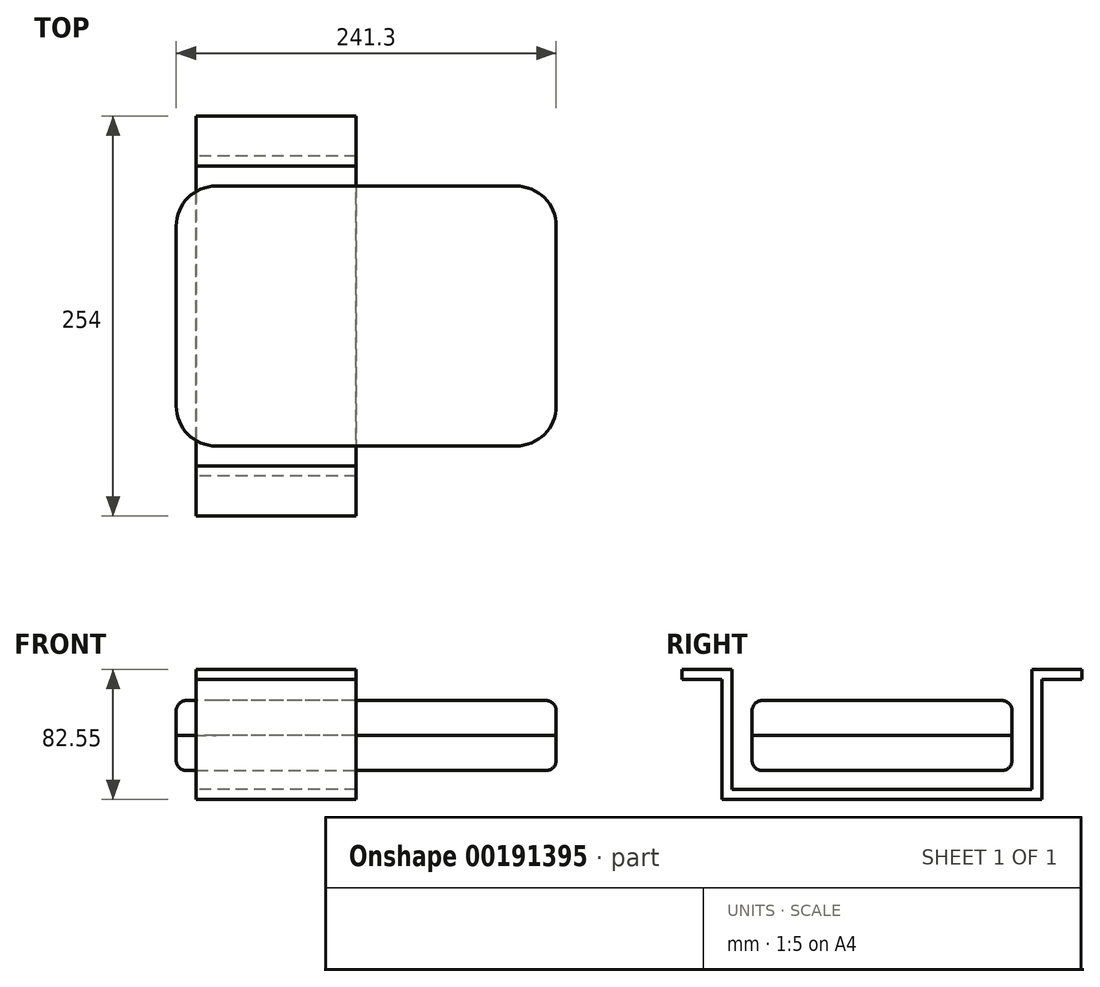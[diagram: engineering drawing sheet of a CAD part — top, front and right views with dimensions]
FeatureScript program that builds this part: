
annotation { "Feature Type Name" : "Feature", "Feature Type Description" : "" }
export const myFeature = defineFeature(function(context is Context, id is Id, definition is map)
    precondition{}
    {
        {
            var Q0;
            Q0=qCreatedBy(makeId("Front.planeOp"),FACE);
            var sketch = newSketch(context, id + "F0", { "sketchPlane" : qUnion([Q0])});
            skLineSegment(sketch, "E0.bottom", {"start": v(-33.91, 0) * mm, "end": v(207.39, 0) * mm});
            skLineSegment(sketch, "E0.top", {"start": v(-33.91, -22.23) * mm, "end": v(207.39, -22.23) * mm});
            skLineSegment(sketch, "E0.left", {"start": v(-33.91, 0) * mm, "end": v(-33.91, -22.22) * mm});
            skLineSegment(sketch, "E0.right", {"start": v(207.39, 0) * mm, "end": v(207.39, -22.22) * mm});
            skSolve(sketch);
        }
        {
            var Q0;
            Q0=makeQuery(id+"F0.imprint","IMPRINT",FACE,{"disambiguationData":[TD([[makeQuery(id+"F0.imprint","IMPRINT",EDGE,{"derivedFrom":sQuery(id+"F0.wireOp",EDGE,"E0.bottom")}),-1.0]])]});
            extrude(context, id + "F1", {"entities" : qUnion([Q0]), "depth" : 165.1 * mm});
        }
        {
            var Q0;
            Q0=makeQuery(id+"F1.opExtrude","CAP_EDGE",EDGE,{"disambiguationData":[OSD([sQuery(id+"F0.wireOp",EDGE,"E0.right")])],"isStart":false});
            var Q1;
            Q1=makeQuery(id+"F1.opExtrude","CAP_EDGE",EDGE,{"disambiguationData":[OSD([sQuery(id+"F0.wireOp",EDGE,"E0.right")])],"isStart":true});
            var Q2;
            Q2=makeQuery(id+"F1.opExtrude","CAP_EDGE",EDGE,{"disambiguationData":[OSD([sQuery(id+"F0.wireOp",EDGE,"E0.left")])],"isStart":false});
            var Q3;
            Q3=makeQuery(id+"F1.opExtrude","CAP_EDGE",EDGE,{"disambiguationData":[OSD([sQuery(id+"F0.wireOp",EDGE,"E0.left")])],"isStart":true});
            fillet(context, id + "F2", {"entities" : qUnion([Q0, Q1, Q2, Q3]), "radius" : 25.4 * mm, "tangentPropagation" : true, "allowEdgeOverflow" : false});
        }
        {
            var Q0;
            Q0=makeQuery(id+"F1.opExtrude","SWEPT_EDGE",EDGE,{"disambiguationData":[OSD([sQuery(id+"F0.wireOp",EDGE,"E0.top"),sQuery(id+"F0.wireOp",EDGE,"E0.right")])]});
            fillet(context, id + "F3", {"entities" : qUnion([Q0]), "radius" : 6.35 * mm, "tangentPropagation" : true, "allowEdgeOverflow" : false});
        }
        {
            var Q0;
            Q0=makeQuery(id+"F1.opExtrude","SWEPT_BODY",BODY,{"disambiguationData":[OSD([sQuery(id+"F0.wireOp",EDGE,"E0.bottom"),sQuery(id+"F0.wireOp",EDGE,"E0.top"),sQuery(id+"F0.wireOp",EDGE,"E0.left"),sQuery(id+"F0.wireOp",EDGE,"E0.right")])]});
            transform(context, id + "F4", {"entities" : qUnion([Q0]), "transformType" : TransformType.TRANSLATION_3D, "dx" : -241.3 * mm, "dy" : 0 * mm, "dz" : 0 * mm, "makeCopy" : true});
        }
        {
            var Q0;
            Q0=makeQuery(id+"F4.opPattern","COPY",BODY,{"derivedFrom":makeQuery(id+"F1.opExtrude","SWEPT_BODY",BODY,{"disambiguationData":[OSD([sQuery(id+"F0.wireOp",EDGE,"E0.bottom"),sQuery(id+"F0.wireOp",EDGE,"E0.top"),sQuery(id+"F0.wireOp",EDGE,"E0.left"),sQuery(id+"F0.wireOp",EDGE,"E0.right")])]}),"instanceName":"1"});
            var Q1;
            Q1=makeQuery(id+"F1.opExtrude","SWEPT_EDGE",EDGE,{"disambiguationData":[OSD([sQuery(id+"F0.wireOp",EDGE,"E0.bottom"),sQuery(id+"F0.wireOp",EDGE,"E0.left")])]});
            transform(context, id + "F5", {"entities" : qUnion([Q0]), "transformType" : TransformType.ROTATION, "transformAxis" : qUnion([Q1]), "angle" : 180 * degree, "makeCopy" : false});
        }
        {
            var Q0;
            Q0=qCreatedBy(makeId("Right.planeOp"),FACE);
            var sketch = newSketch(context, id + "F6", { "sketchPlane" : qUnion([Q0])});
            skLineSegment(sketch, "E1", {"start": v(19.05, -40.55) * mm, "end": v(19.05, 35.65) * mm});
            skLineSegment(sketch, "E2", {"start": v(19.05, 35.65) * mm, "end": v(44.45, 35.65) * mm});
            skLineSegment(sketch, "E3", {"start": v(44.45, 35.65) * mm, "end": v(44.45, 42) * mm});
            skLineSegment(sketch, "E4", {"start": v(44.45, 42) * mm, "end": v(12.7, 42) * mm});
            skLineSegment(sketch, "E5", {"start": v(12.7, 42) * mm, "end": v(12.7, -34.2) * mm});
            skLineSegment(sketch, "E6", {"start": v(12.7, -34.2) * mm, "end": v(-177.8, -34.2) * mm});
            skLineSegment(sketch, "E7", {"start": v(-177.8, -34.2) * mm, "end": v(-177.8, 42) * mm});
            skLineSegment(sketch, "E8", {"start": v(-177.8, 42) * mm, "end": v(-209.55, 42) * mm});
            skLineSegment(sketch, "E9", {"start": v(-209.55, 42) * mm, "end": v(-209.55, 35.65) * mm});
            skLineSegment(sketch, "E10", {"start": v(-209.55, 35.65) * mm, "end": v(-184.15, 35.65) * mm});
            skLineSegment(sketch, "E11", {"start": v(-184.15, 35.65) * mm, "end": v(-184.15, -40.55) * mm});
            skLineSegment(sketch, "E12", {"start": v(-184.15, -40.55) * mm, "end": v(19.05, -40.55) * mm});
            skSolve(sketch);
        }
        {
            var Q0;
            Q0=makeQuery(id+"F6.imprint","IMPRINT",FACE,{"disambiguationData":[TD([[makeQuery(id+"F6.imprint","IMPRINT",EDGE,{"derivedFrom":sQuery(id+"F6.wireOp",EDGE,"E1")}),1.0]])]});
            extrude(context, id + "F7", {"entities" : qUnion([Q0]), "depth" : 101.6 * mm});
        }
        {
            var Q0;
            Q0=makeQuery(id+"F1.opExtrude","SWEPT_BODY",BODY,{"disambiguationData":[OSD([sQuery(id+"F0.wireOp",EDGE,"E0.bottom"),sQuery(id+"F0.wireOp",EDGE,"E0.top"),sQuery(id+"F0.wireOp",EDGE,"E0.left"),sQuery(id+"F0.wireOp",EDGE,"E0.right")])]});
            var Q1;
            Q1=makeQuery(id+"F4.opPattern","COPY",BODY,{"derivedFrom":makeQuery(id+"F1.opExtrude","SWEPT_BODY",BODY,{"disambiguationData":[OSD([sQuery(id+"F0.wireOp",EDGE,"E0.bottom"),sQuery(id+"F0.wireOp",EDGE,"E0.top"),sQuery(id+"F0.wireOp",EDGE,"E0.left"),sQuery(id+"F0.wireOp",EDGE,"E0.right")])]}),"instanceName":"1"});
            transform(context, id + "F8", {"entities" : qUnion([Q0, Q1]), "transformType" : TransformType.TRANSLATION_3D, "dx" : 33.9 * mm, "dy" : 0 * mm, "dz" : 0 * mm, "makeCopy" : false});
        }
        {
            var Q0;
            Q0=makeQuery(id+"F1.opExtrude","SWEPT_BODY",BODY,{"disambiguationData":[OSD([sQuery(id+"F0.wireOp",EDGE,"E0.bottom"),sQuery(id+"F0.wireOp",EDGE,"E0.top"),sQuery(id+"F0.wireOp",EDGE,"E0.left"),sQuery(id+"F0.wireOp",EDGE,"E0.right")])]});
            var Q1;
            Q1=makeQuery(id+"F4.opPattern","COPY",BODY,{"derivedFrom":makeQuery(id+"F1.opExtrude","SWEPT_BODY",BODY,{"disambiguationData":[OSD([sQuery(id+"F0.wireOp",EDGE,"E0.bottom"),sQuery(id+"F0.wireOp",EDGE,"E0.top"),sQuery(id+"F0.wireOp",EDGE,"E0.left"),sQuery(id+"F0.wireOp",EDGE,"E0.right")])]}),"instanceName":"1"});
            transform(context, id + "F9", {"entities" : qUnion([Q0, Q1]), "transformType" : TransformType.TRANSLATION_3D, "dx" : -12.7 * mm, "dy" : 0 * mm, "dz" : 0 * mm, "makeCopy" : false});
        }
    });
